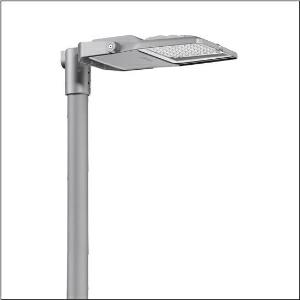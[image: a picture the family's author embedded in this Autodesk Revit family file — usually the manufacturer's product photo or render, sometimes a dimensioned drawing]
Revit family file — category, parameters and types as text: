
# Revit family: floodlight_fl_21_iq_mini___pl43_5xa7772b2a3a_a256
name_source: partatom
category: Lighting Fixtures
units: mm (PartAtom-declared; Revit-internal decimal feet)

## family parameters
Cut with Voids When Loaded = No
Host = Face
Light Source = No
Part Type = Normal
Room Calculation Point = No
Round Connector Dimension = Use Diameter
Shared = No

## types (1)
- --- (1 x LED, 6400 lm, 45.5 W, 3000K)
    Apparent Load = 46 VA
    CIE Flux Codes = 27 78 99 100 100
    Color Rendering = 70
    Color Temperature = 3000K
    Default Elevation = 1800 mm
    Description = Floodlight FL 21 iQ mini, floodlight, primary light control with lens, of PMMA, primary optical cover: protective disc, of toughened safety glass, transparent, light distribution: PL43, light emission: direct distribution, installation type: surface-mounted, LED, High Power LED, rated luminous flux: 6.400lm, luminous efficacy: 141lm/W, light colour: 730, colour temperature: 3000K, control: Auto-Match, Temp-Guard, Night-Set, Smart-Wire, Desk-Remote (wireless, voltage-free reading and setting of iQ features in the workshop via application-optimized NFC function/RFID function), optimised constant luminous flux control (CLO 2.0), Light-Fading, Lumen-Switch, with terminal, 6-pole, mains connection: 220..240V, AC, 50/60Hz, start of lifetime: 46W, end of service life: 48W, reduction: 22W, luminaire housing, of diecast aluminium, powder-coated, Siteco® metallic grey (DB 702S), corrosivity category C5 mid according to DIN EN ISO 12944, sealing non-destructively replaceable, please order mast flange separately, mast bracket, of steel, galvanised, powder-coated, protection rating (complete): IP66, insulation class (complete): insulation class II (safety insulation), certification: CE, ENEC, VDE, protection symbol: D, impact resistance: IK08, permissible operating ambient temperature: -40..+40°C, permissible operating ambient temperature for outdoor applications: -40..+50°C, standard: DIN EN 12944, LABS conformity tested according to VDMA 24364:2018-05, packaging unit: 1 piece

Light Distribution: PL43
    Height = 70 mm
    Lamp = 1 x LED
    Lamp Light Flux = 6400 lm
    Lamp Power = 45.5 W
    Lamp count = 1
    Length = 485 mm
    Luminous efficacy = 141 lm/W
    Manufacturer = Siteco
    ModVariant = No
    Model = 5XA7772B2A3A
    Number of Poles = 1
    OnlyDefault = Yes
    Power Factor = 1
    Product Name = Floodlight FL 21 iQ mini | PL43
    Product group = floodlight | pylon annexe
    ProductGroupID = 6200
    Protection Class = Protection class II
    Protection Degree = IP 66
    RLX_Detail_Level = 1
    RLX_Emergency_Light_Flux = 0 lm
    RLX_Emergency_Type = 0
    RLX_Emergency_Type_DB = No
    RlxData = <blob elided: 101113 chars, md5=3b119b11>
    Socket = socket
    Standby Power = 0 W
    System Light Flux = 6400 lm
    System Power = 46 W
    Type Comments = factory setting: luminous flux: 100 % | dim-lin: 254 | 463 mA
    Type Image = l_1007125.jpg
    URL = http://relux.com
    VarID = @adj_133123
    Voltage = 0 V
    Weight = 0.00 kg
    Width = 337 mm

## geometry (parser evidence)
native form markers: Blend x4, Sweep x12
no freeform markers — native parametric forms only
